# Revit family: 4410S_Single Hung Steel Replica
name_source: partatom
category: Windows
units: mm (PartAtom-declared; Revit-internal decimal feet)

## family parameters
Always vertical = Yes
Cut with Voids When Loaded = No
Host = Wall
OmniClass Number = 23.30.20.00
OmniClass Title = Windows
Room Calculation Point = No
Shared = No

## types (1)
- 4410S_Single Hung Steel Replica
    Bottom Bay Horizontal Member Array = 2
    Bottom Bay Horizontal Member Array Vis = Yes
    Bottom Bay Single Horizontal Member Vis = Yes
    Bottom Bay Single Vertical Member Vis = Yes
    Bottom Bay Vertical Member Array = 2
    Bottom Bay Vertical Member Array Vis = Yes
    Default Sill Height = 3' - 0"
    Depth From Exterior = 0' - 1"
    Equal Bay Height = 0' - 8 29/32"
    Equal Bay Width = 0' - 9 17/32"
    Frame Material = <By Category>
    Glass Material = Glass
    Height = 5' - 0"
    Horizontal Member Length = 2' - 5 5/16"
    Keep Rail Mid = 2' - 5 5/16"
    Keep Top Bay Horizontal Member Mid = 1' - 1 9/16"
    Keep Vertical Member Mid = 1' - 5 27/32"
    Top Bay Horizontal Member Array = 2
    Top Bay Horizontal Member Array Vis = No
    Top Bay Single Horizontal Member Vis = No
    Top Bay Single Vertical Member Vis = No
    Top Bay Vertical Member Array = 2
    Top Bay Vertical Member Array Vis = Yes
    Vent Height = 2' - 4 5/8"
    Vent Width = 2' - 7"
    Vertical Member Length = 2' - 3 7/16"
    Wall Closure = By host
    Width = 3' - 0"

## geometry (parser evidence)
native form markers: Sweep x14
no freeform markers — native parametric forms only
